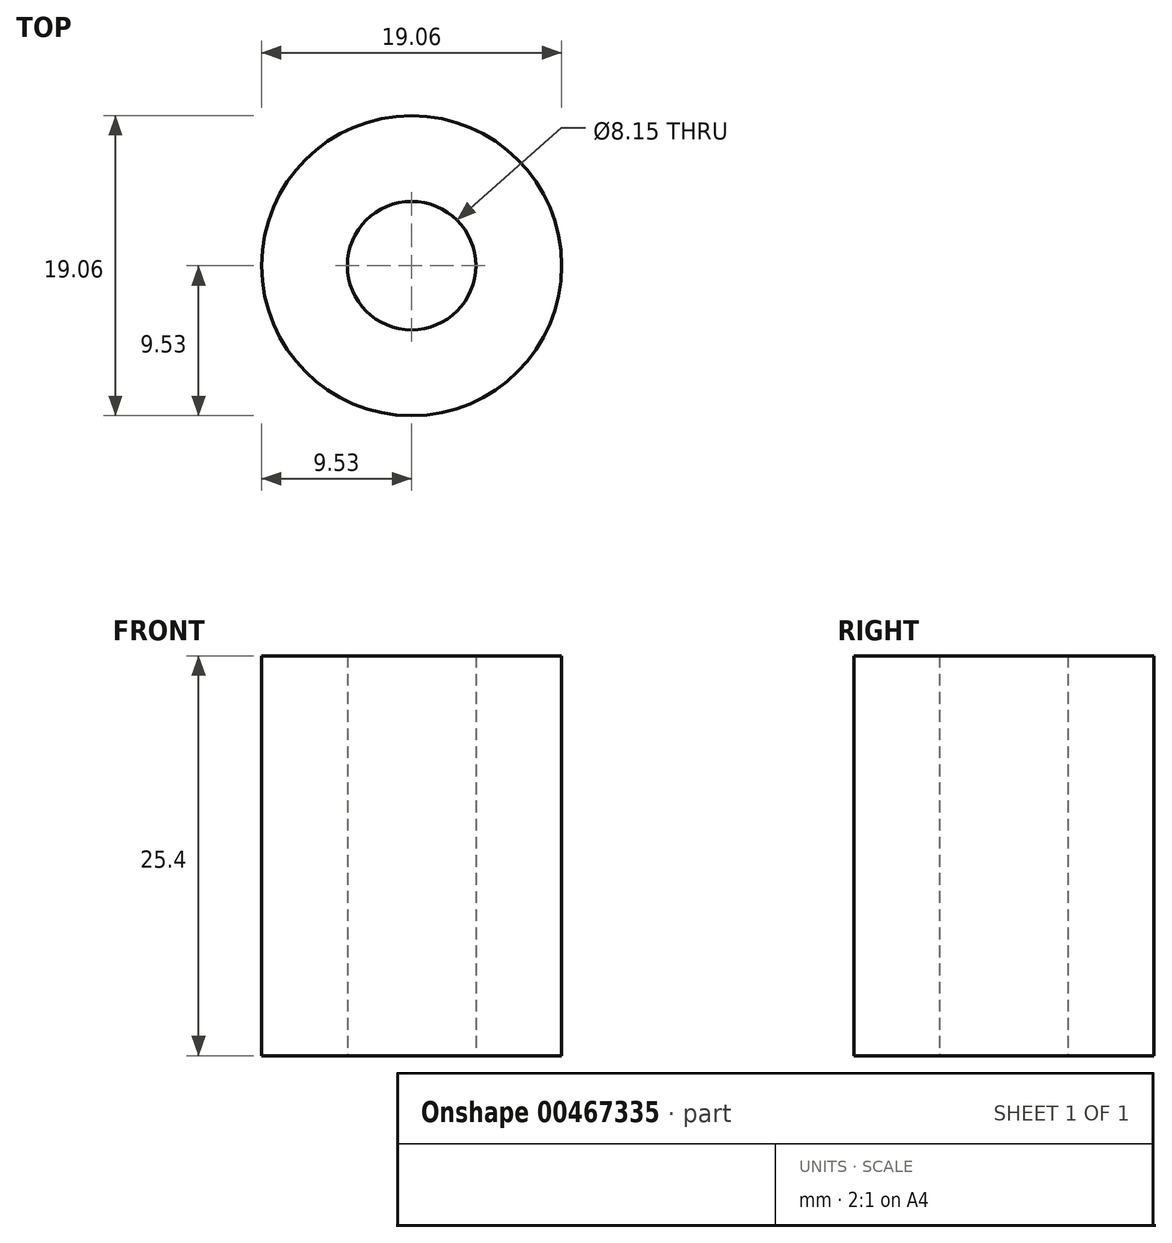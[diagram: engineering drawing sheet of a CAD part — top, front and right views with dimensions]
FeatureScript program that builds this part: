
annotation { "Feature Type Name" : "Feature", "Feature Type Description" : "" }
export const myFeature = defineFeature(function(context is Context, id is Id, definition is map)
    precondition{}
    {
        {
            var Q0;
            Q0=qCreatedBy(makeId("Top.planeOp"),FACE);
            var sketch = newSketch(context, id + "F0", { "sketchPlane" : qUnion([Q0])});
            skCircle(sketch, "E0", {"center": v(0, 0) * mm, "radius": 9.53 * mm});
            skCircle(sketch, "E1", {"center": v(0, 0) * mm, "radius": 4.08 * mm});
            skSolve(sketch);
        }
        {
            var Q0;
            Q0=makeQuery(id+"F0.imprint","IMPRINT",FACE,{"disambiguationData":[TD([[makeQuery(id+"F0.imprint","IMPRINT",EDGE,{"derivedFrom":sQuery(id+"F0.wireOp",EDGE,"E0")}),1.0]])]});
            extrude(context, id + "F1", {"entities" : qUnion([Q0]), "depth" : 25.4 * mm});
        }
    });
